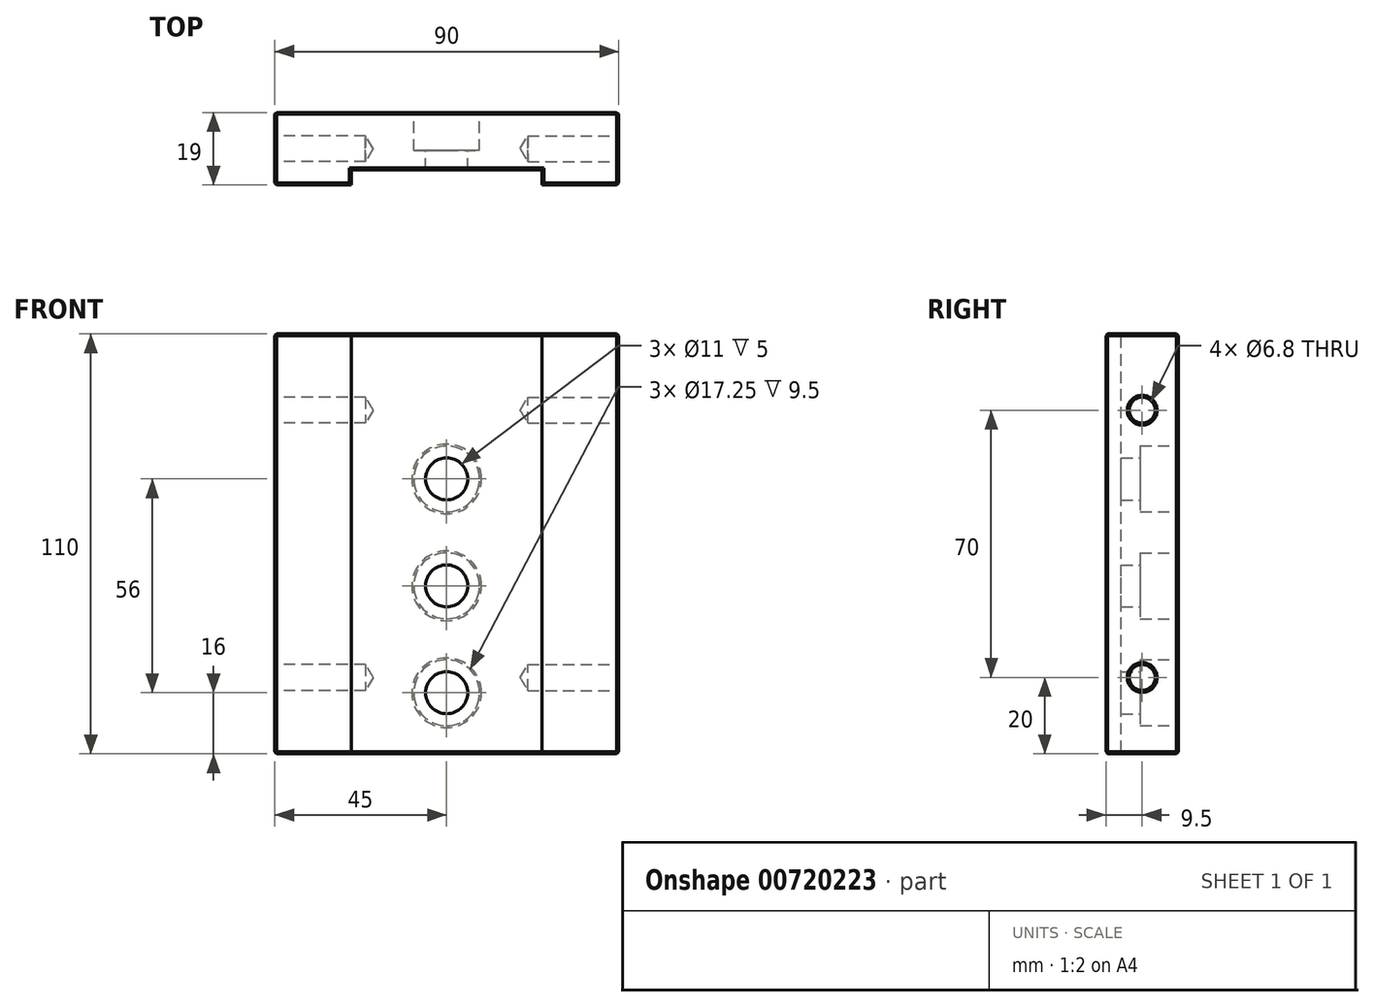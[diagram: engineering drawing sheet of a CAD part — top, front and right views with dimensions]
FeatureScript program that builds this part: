
annotation { "Feature Type Name" : "Feature", "Feature Type Description" : "" }
export const myFeature = defineFeature(function(context is Context, id is Id, definition is map)
    precondition{}
    {
        {
            var Q0;
            Q0=qCreatedBy(makeId("Front.planeOp"),FACE);
            var sketch = newSketch(context, id + "F0", { "sketchPlane" : qUnion([Q0])});
            skLineSegment(sketch, "E0.bottom", {"start": v(0, 0) * mm, "end": v(-90, 0) * mm});
            skLineSegment(sketch, "E0.top", {"start": v(0, 110) * mm, "end": v(-90, 110) * mm});
            skLineSegment(sketch, "E0.left", {"start": v(0, 0) * mm, "end": v(0, 110) * mm});
            skLineSegment(sketch, "E0.right", {"start": v(-90, 0) * mm, "end": v(-90, 110) * mm});
            skSolve(sketch);
        }
        {
            var Q0;
            Q0 = qSketchRegion(id + "F0", true);
            extrude(context, id + "F1", {"entities" : qUnion([Q0]), "depth" : 19 * mm, "offsetDistance" : 25 * mm});
        }
        {
            var Q0;
            Q0=makeQuery(id+"F1.opExtrude","CAP_FACE",FACE,{"disambiguationData":[OSD([sQuery(id+"F0.wireOp",EDGE,"E0.bottom"),sQuery(id+"F0.wireOp",EDGE,"E0.top"),sQuery(id+"F0.wireOp",EDGE,"E0.left"),sQuery(id+"F0.wireOp",EDGE,"E0.right")])],"isStart":false});
            var sketch = newSketch(context, id + "F2", { "sketchPlane" : qUnion([Q0])});
            skPoint(sketch, "E1", {"position": v(-70, 0) * mm});
            skLineSegment(sketch, "E2.bottom", {"start": v(-70, 0) * mm, "end": v(-20, 0) * mm});
            skLineSegment(sketch, "E2.top", {"start": v(-70, 110) * mm, "end": v(-20, 110) * mm});
            skLineSegment(sketch, "E2.left", {"start": v(-70, 0) * mm, "end": v(-70, 110) * mm});
            skLineSegment(sketch, "E2.right", {"start": v(-20, 0) * mm, "end": v(-20, 110) * mm});
            skSolve(sketch);
        }
        {
            var Q0;
            Q0 = qSketchRegion(id + "F2", true);
            extrude(context, id + "F3", {"entities" : qUnion([Q0]), "operationType" : NewBodyOperationType.REMOVE, "oppositeDirection" : true, "depth" : 4 * mm, "offsetDistance" : 25 * mm});
        }
        {
            var Q0;
            Q0=makeQuery(id+"F1.opExtrude","CAP_FACE",FACE,{"disambiguationData":[OSD([sQuery(id+"F0.wireOp",EDGE,"E0.bottom"),sQuery(id+"F0.wireOp",EDGE,"E0.top"),sQuery(id+"F0.wireOp",EDGE,"E0.left"),sQuery(id+"F0.wireOp",EDGE,"E0.right")])],"isStart":true});
            var sketch = newSketch(context, id + "F4", { "sketchPlane" : qUnion([Q0])});
            skPoint(sketch, "E3", {"position": v(45, 16) * mm});
            skPoint(sketch, "E3.positionSnap0", {"position": v(45, 0) * mm});
            skPoint(sketch, "E4", {"position": v(45, 44) * mm});
            skPoint(sketch, "E5", {"position": v(45, 72) * mm});
            skSolve(sketch);
        }
        {
            var Q0;
            Q0=sQuery(id+"F4.wireOp",VERTEX,"E5");
            var Q1;
            Q1=sQuery(id+"F4.wireOp",VERTEX,"E4");
            var Q2;
            Q2=sQuery(id+"F4.wireOp",VERTEX,"E3");
            var Q3;
            Q3=makeQuery(id+"F1.opExtrude","SWEPT_BODY",BODY,{"disambiguationData":[OSD([sQuery(id+"F0.wireOp",EDGE,"E0.bottom"),sQuery(id+"F0.wireOp",EDGE,"E0.top"),sQuery(id+"F0.wireOp",EDGE,"E0.left"),sQuery(id+"F0.wireOp",EDGE,"E0.right")])]});
            hole(context, id + "F5", {"style" : HoleStyle.C_BORE, "endStyle" : HoleEndStyle.THROUGH, "standardTappedOrClearance" : lookupTablePath({ "standard" : "ISO", "fit" : "Normal", "size" : "M10", "type" : "Clearance" }), "standardBlindInLast" : lookupTablePath({ "fit" : "Standard", "standard" : "ISO", "size" : "M10", "type" : "Clearance" }), "holeDiameter" : 11 * mm, "cBoreDiameter" : 17.25 * mm, "cBoreDepth" : 10 * mm, "majorDiameter" : 5 * mm, "isTappedThrough" : true, "tappedDepth" : 17.25 * mm, "tapClearance" : 3, "locations" : qUnion([Q0, Q1, Q2]), "scope" : qUnion([Q3])});
        }
        {
            var Q0;
            Q0=makeQuery(id+"F1.opExtrude","SWEPT_FACE",FACE,{"disambiguationData":[OSD([sQuery(id+"F0.wireOp",EDGE,"E0.left")])]});
            var sketch = newSketch(context, id + "F6", { "sketchPlane" : qUnion([Q0])});
            skPoint(sketch, "E6", {"position": v(-9.5, 0) * mm});
            skPoint(sketch, "E7", {"position": v(-9.5, 20) * mm});
            skPoint(sketch, "E8", {"position": v(-9.5, 90) * mm});
            skSolve(sketch);
        }
        {
            var Q0;
            Q0=makeQuery(id+"F1.opExtrude","SWEPT_FACE",FACE,{"disambiguationData":[OSD([sQuery(id+"F0.wireOp",EDGE,"E0.right")])]});
            var sketch = newSketch(context, id + "F7", { "sketchPlane" : qUnion([Q0])});
            skPoint(sketch, "E9", {"position": v(9.5, 90) * mm});
            skPoint(sketch, "E9.positionSnap0", {"position": v(9.5, 110) * mm});
            skPoint(sketch, "E10", {"position": v(9.5, 20) * mm});
            skPoint(sketch, "E10.positionSnap0", {"position": v(9.5, 0) * mm});
            skSolve(sketch);
        }
        {
            var Q0;
            Q0=sQuery(id+"F6.wireOp",VERTEX,"E8");
            var Q1;
            Q1=sQuery(id+"F6.wireOp",VERTEX,"E7");
            var Q2;
            Q2=sQuery(id+"F7.wireOp",VERTEX,"E9");
            var Q3;
            Q3=sQuery(id+"F7.wireOp",VERTEX,"E10");
            var Q4;
            Q4=makeQuery(id+"F1.opExtrude","SWEPT_BODY",BODY,{"disambiguationData":[OSD([sQuery(id+"F0.wireOp",EDGE,"E0.bottom"),sQuery(id+"F0.wireOp",EDGE,"E0.top"),sQuery(id+"F0.wireOp",EDGE,"E0.left"),sQuery(id+"F0.wireOp",EDGE,"E0.right")])]});
            hole(context, id + "F8", {"style" : HoleStyle.SIMPLE, "endStyle" : HoleEndStyle.BLIND, "standardTappedOrClearance" : lookupTablePath({ "standard" : "ISO", "engagement" : "75%", "pitch" : "1.25 mm", "size" : "M8", "type" : "Tapped" }), "standardBlindInLast" : lookupTablePath({ "standard" : "ISO", "engagement" : "75%", "pitch" : "1.25 mm", "size" : "M8", "type" : "Tapped" }), "holeDiameter" : 6.8 * mm, "majorDiameter" : 8 * mm, "showTappedDepth" : true, "holeDepth" : 23.75 * mm, "isTappedThrough" : true, "tappedDepth" : 20 * mm, "tapClearance" : 3, "locations" : qUnion([Q0, Q1, Q2, Q3]), "scope" : qUnion([Q4])});
        }
        {
            var Q0;
            Q0=makeQuery(id+"F1.opExtrude","SWEPT_FACE",FACE,{"disambiguationData":[OSD([sQuery(id+"F0.wireOp",EDGE,"E0.top")])]});
            var Q1;
            Q1=makeQuery(id+"F1.opExtrude","SWEPT_FACE",FACE,{"disambiguationData":[OSD([sQuery(id+"F0.wireOp",EDGE,"E0.bottom")])]});
            var Q2;
            Q2=makeQuery(id+"F1.opExtrude","SWEPT_FACE",FACE,{"disambiguationData":[OSD([sQuery(id+"F0.wireOp",EDGE,"E0.left")])]});
            var Q3;
            Q3=makeQuery(id+"F1.opExtrude","SWEPT_FACE",FACE,{"disambiguationData":[OSD([sQuery(id+"F0.wireOp",EDGE,"E0.right")])]});
            var Q4;
            Q4=makeQuery(id+"F1.opExtrude","CAP_FACE",FACE,{"disambiguationData":[OSD([sQuery(id+"F0.wireOp",EDGE,"E0.bottom"),sQuery(id+"F0.wireOp",EDGE,"E0.top"),sQuery(id+"F0.wireOp",EDGE,"E0.left"),sQuery(id+"F0.wireOp",EDGE,"E0.right")])],"isStart":true});
            chamfer(context, id + "F9", {"entities" : qUnion([Q0, Q1, Q2, Q3, Q4]), "width" : .5 * mm, "tangentPropagation" : true});
        }
    });
